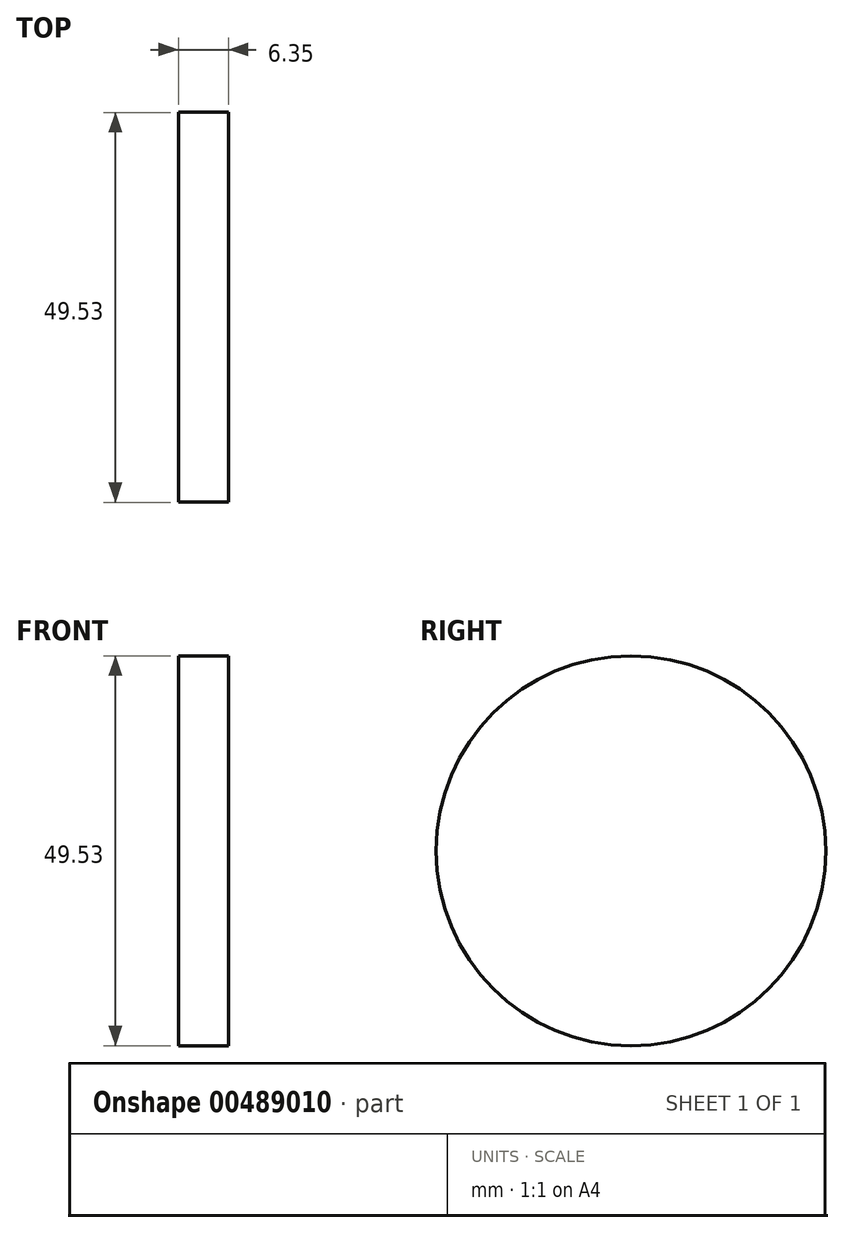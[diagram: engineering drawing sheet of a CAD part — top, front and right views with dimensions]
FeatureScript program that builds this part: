
annotation { "Feature Type Name" : "Feature", "Feature Type Description" : "" }
export const myFeature = defineFeature(function(context is Context, id is Id, definition is map)
    precondition{}
    {
        {
            var Q0;
            Q0=qCreatedBy(makeId("Right.planeOp"),FACE);
            var sketch = newSketch(context, id + "F0", { "sketchPlane" : qUnion([Q0])});
            skCircle(sketch, "E0", {"center": v(-2.65, 22.41) * mm, "radius": 24.77 * mm});
            skSolve(sketch);
        }
        {
            var Q0;
            Q0=makeQuery(id+"F0.imprint","IMPRINT",FACE,{"disambiguationData":[TD([[makeQuery(id+"F0.imprint","IMPRINT",EDGE,{"derivedFrom":sQuery(id+"F0.wireOp",EDGE,"E0")}),1.0]])]});
            extrude(context, id + "F1", {"entities" : qUnion([Q0]), "depth" : 6.35 * mm});
        }
    });
